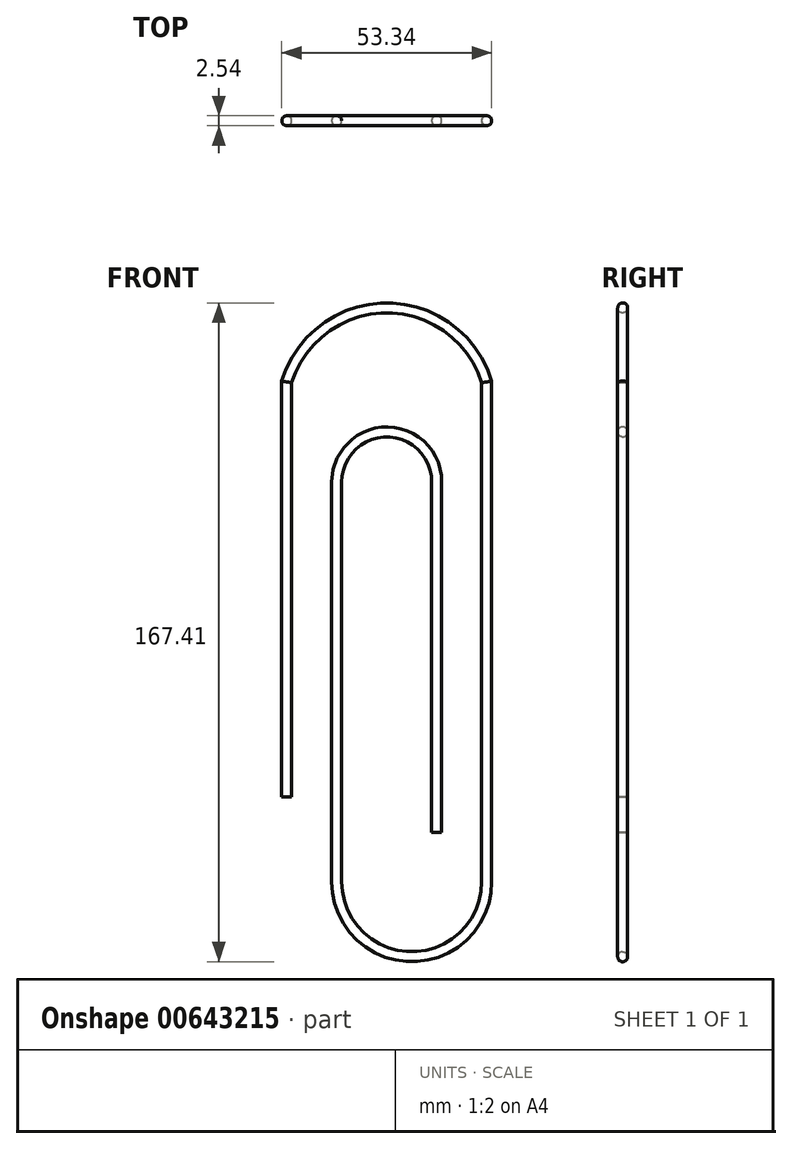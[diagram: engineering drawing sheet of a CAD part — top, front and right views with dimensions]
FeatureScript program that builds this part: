
annotation { "Feature Type Name" : "Feature", "Feature Type Description" : "" }
export const myFeature = defineFeature(function(context is Context, id is Id, definition is map)
    precondition{}
    {
        {
            var Q0;
            Q0=qCreatedBy(makeId("Front.planeOp"),FACE);
            var sketch = newSketch(context, id + "F0", { "sketchPlane" : qUnion([Q0])});
            skLineSegment(sketch, "E0", {"start": v(0, 105.41) * mm, "end": v(0, 0) * mm});
            skLineSegment(sketch, "E1", {"start": v(12.7, 80.01) * mm, "end": v(12.7, -21.59) * mm});
            skLineSegment(sketch, "E2", {"start": v(38.1, 80.01) * mm, "end": v(38.1, -9) * mm});
            skLineSegment(sketch, "E3", {"start": v(50.8, 105.41) * mm, "end": v(50.8, -21.59) * mm});
            skArc(sketch, "E4", {"start": v(50.8, 105.41) * mm, "mid": v(25.4, 124.23) * mm, "end": v(0, 105.41) * mm});
            skArc(sketch, "E5", {"start": v(38.1, 80.01) * mm, "mid": v(25.4, 92.71) * mm, "end": v(12.7, 80.01) * mm});
            skArc(sketch, "E6", {"start": v(12.7, -21.59) * mm, "mid": v(31.75, -40.64) * mm, "end": v(50.8, -21.59) * mm});
            skLineSegment(sketch, "E7", {"start": v(77.82, -21.59) * mm, "end": v(-31.4, -21.59) * mm, "construction": true});
            skLineSegment(sketch, "E8", {"start": v(63, 105.41) * mm, "end": v(-111.13, 105.41) * mm, "construction": true});
            skSolve(sketch);
        }
        {
            var Q0;
            Q0=qCreatedBy(makeId("Top.planeOp"),FACE);
            var sketch = newSketch(context, id + "F1", { "sketchPlane" : qUnion([Q0])});
            skCircle(sketch, "E9", {"center": v(0, 0) * mm, "radius": 1.27 * mm});
            skSolve(sketch);
        }
        {
            var Q0;
            Q0 = qSketchRegion(id + "F1", true);
            var Q1;
            Q1 = qConstructionFilter(qBodyType(qCreatedBy(id + "F0" ,EDGE), BodyType.WIRE), ConstructionObject.NO);
            sweep(context, id + "F2", {"profiles" : qUnion([Q0]), "path" : qUnion([Q1])});
        }
    });
